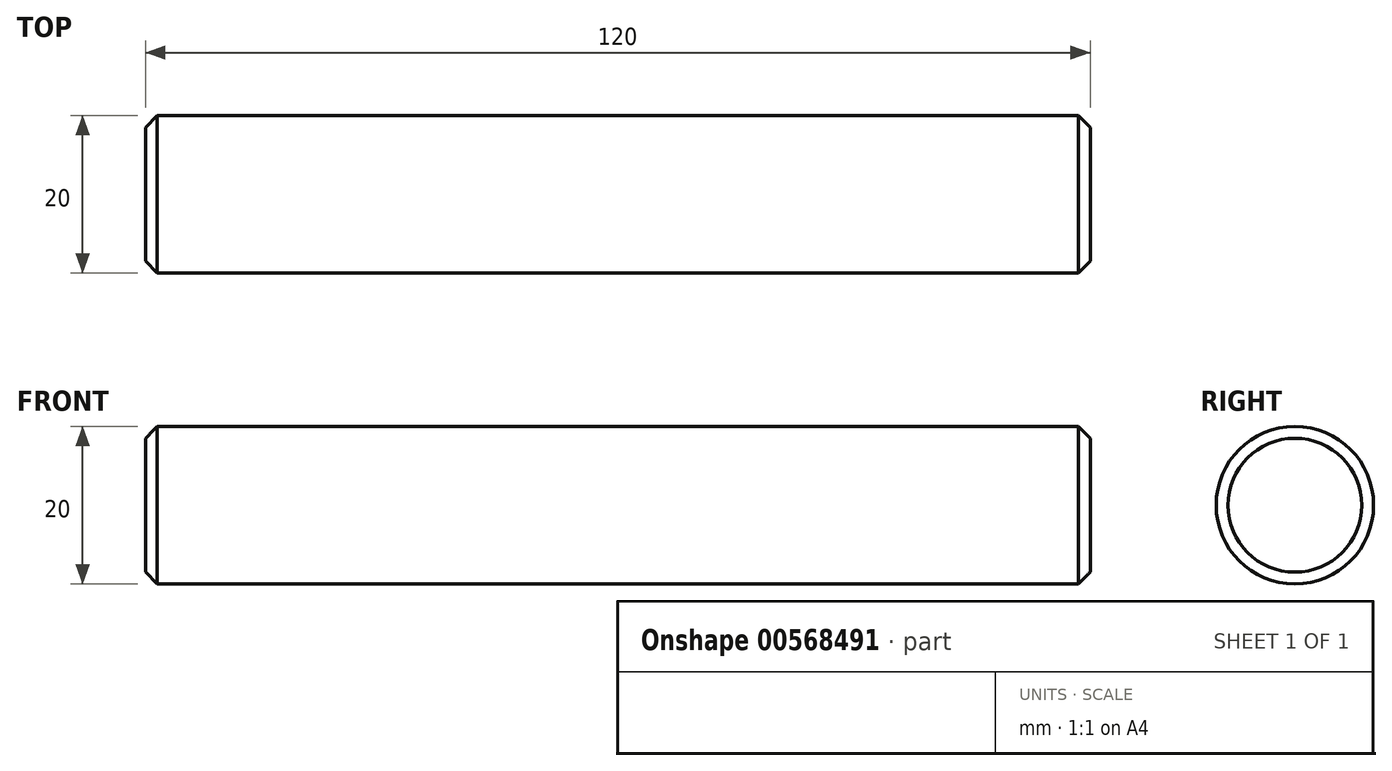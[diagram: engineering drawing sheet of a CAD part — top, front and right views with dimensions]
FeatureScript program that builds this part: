
annotation { "Feature Type Name" : "Feature", "Feature Type Description" : "" }
export const myFeature = defineFeature(function(context is Context, id is Id, definition is map)
    precondition{}
    {
        {
            var Q0;
            Q0=qCreatedBy(makeId("Top.planeOp"),FACE);
            var sketch = newSketch(context, id + "F0", { "sketchPlane" : qUnion([Q0])});
            skLineSegment(sketch, "E0", {"start": v(0, 0) * mm, "end": v(-120, 0) * mm, "construction": true});
            skLineSegment(sketch, "E1", {"start": v(-120, 0) * mm, "end": v(-120, -10) * mm});
            skLineSegment(sketch, "E2", {"start": v(-120, -10) * mm, "end": v(0, -10) * mm});
            skLineSegment(sketch, "E3", {"start": v(0, -10) * mm, "end": v(0, 0) * mm});
            skSolve(sketch);
        }
        {
            var Q0;
            Q0=sQuery(id+"F0.wireOp",EDGE,"E1");
            var Q1;
            Q1=sQuery(id+"F0.wireOp",EDGE,"E2");
            var Q2;
            Q2=sQuery(id+"F0.wireOp",EDGE,"E3");
            var Q3;
            Q3=sQuery(id+"F0.wireOp",EDGE,"E0");
            revolve(context, id + "F1", {"bodyType" : ToolBodyType.SURFACE, "surfaceEntities" : qUnion([Q0, Q1, Q2]), "axis" : qUnion([Q3]), "revolveType" : RevolveType.FULL});
        }
        {
            var Q0;
            Q0=makeQuery(id+"F1.opRevolve","SWEPT_EDGE",EDGE,{"disambiguationData":[OSD([sQuery(id+"F0.wireOp",VERTEX,"E2.start")])]});
            var Q1;
            Q1=makeQuery(id+"F1.opRevolve","SWEPT_EDGE",EDGE,{"disambiguationData":[OSD([sQuery(id+"F0.wireOp",VERTEX,"E3.start")])]});
            chamfer(context, id + "F2", {"entities" : qUnion([Q0, Q1]), "width" : 1.5 * mm, "tangentPropagation" : true});
        }
    });
